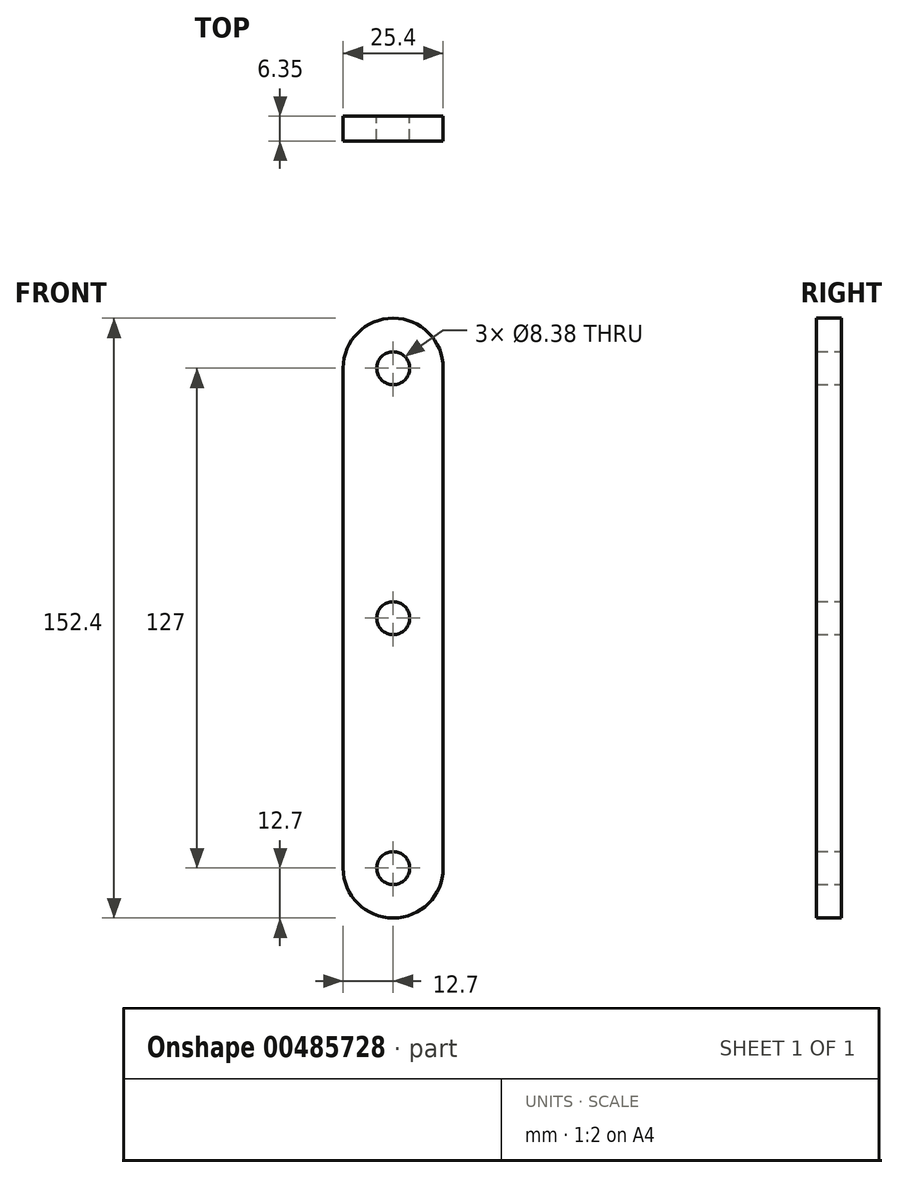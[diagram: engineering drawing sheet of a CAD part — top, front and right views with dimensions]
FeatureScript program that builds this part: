
annotation { "Feature Type Name" : "Feature", "Feature Type Description" : "" }
export const myFeature = defineFeature(function(context is Context, id is Id, definition is map)
    precondition{}
    {
        {
            var Q0;
            Q0=qCreatedBy(makeId("Front.planeOp"),FACE);
            var sketch = newSketch(context, id + "F0", { "sketchPlane" : qUnion([Q0])});
            skLineSegment(sketch, "E0.bottom", {"start": v(12.7, 63.5) * mm, "end": v(-12.7, 63.5) * mm});
            skLineSegment(sketch, "E0.top", {"start": v(12.7, -63.5) * mm, "end": v(-12.7, -63.5) * mm});
            skLineSegment(sketch, "E0.left", {"start": v(12.7, 63.5) * mm, "end": v(12.7, -63.5) * mm});
            skLineSegment(sketch, "E0.right", {"start": v(-12.7, 63.5) * mm, "end": v(-12.7, -63.5) * mm});
            skPoint(sketch, "E0.middle", {"position": v(0, 0) * mm});
            skPoint(sketch, "E1", {"position": v(0, 63.5) * mm});
            skPoint(sketch, "E2", {"position": v(0, -63.5) * mm});
            skCircle(sketch, "E3", {"center": v(0, 63.5) * mm, "radius": 12.7 * mm});
            skCircle(sketch, "E4", {"center": v(0, -63.5) * mm, "radius": 12.7 * mm});
            skCircle(sketch, "E5", {"center": v(0, -63.5) * mm, "radius": 4.2 * mm});
            skCircle(sketch, "E6", {"center": v(0, 0) * mm, "radius": 4.2 * mm});
            skCircle(sketch, "E7", {"center": v(0, 63.5) * mm, "radius": 4.2 * mm});
            skSolve(sketch);
        }
        {
            var Q0;
            {var subQ1=sQuery(id+"F0.wireOp",EDGE,"E0.bottom");var subQ3=sQuery(id+"F0.wireOp",EDGE,"E7");var subQ4=makeQuery(id+"F0.imprint","INTERSECT",VERTEX,{"disambiguationData":[OD(0.0)],"derivedFrom":[subQ1,subQ3]});Q0=makeQuery(id+"F0.imprint","IMPRINT",FACE,{"disambiguationData":[TD([[makeQuery(id+"F0.imprint","IMPRINT",EDGE,{"disambiguationData":[TD([[subQ4,1.0]])],"derivedFrom":subQ3}),-1.0]])]});}
            var Q1;
            {var subQ1=sQuery(id+"F0.wireOp",EDGE,"E0.bottom");var subQ3=sQuery(id+"F0.wireOp",EDGE,"E7");var subQ4=makeQuery(id+"F0.imprint","INTERSECT",VERTEX,{"disambiguationData":[OD(0.0)],"derivedFrom":[subQ1,subQ3]});Q1=makeQuery(id+"F0.imprint","IMPRINT",FACE,{"disambiguationData":[TD([[makeQuery(id+"F0.imprint","IMPRINT",EDGE,{"disambiguationData":[TD([[subQ4,-1.0]])],"derivedFrom":subQ3}),-1.0]])]});}
            var Q2;
            {var subQ1=sQuery(id+"F0.wireOp",EDGE,"E0.left");Q2=makeQuery(id+"F0.imprint","IMPRINT",FACE,{"disambiguationData":[TD([[makeQuery(id+"F0.imprint","IMPRINT",EDGE,{"derivedFrom":subQ1}),-1.0]])]});}
            var Q3;
            {var subQ1=sQuery(id+"F0.wireOp",EDGE,"E0.top");var subQ3=sQuery(id+"F0.wireOp",EDGE,"E5");var subQ4=makeQuery(id+"F0.imprint","INTERSECT",VERTEX,{"disambiguationData":[OD(0.0)],"derivedFrom":[subQ1,subQ3]});Q3=makeQuery(id+"F0.imprint","IMPRINT",FACE,{"disambiguationData":[TD([[makeQuery(id+"F0.imprint","IMPRINT",EDGE,{"disambiguationData":[TD([[subQ4,-1.0]])],"derivedFrom":subQ3}),-1.0]])]});}
            var Q4;
            {var subQ1=sQuery(id+"F0.wireOp",EDGE,"E0.top");var subQ3=sQuery(id+"F0.wireOp",EDGE,"E5");var subQ4=makeQuery(id+"F0.imprint","INTERSECT",VERTEX,{"disambiguationData":[OD(0.0)],"derivedFrom":[subQ1,subQ3]});Q4=makeQuery(id+"F0.imprint","IMPRINT",FACE,{"disambiguationData":[TD([[makeQuery(id+"F0.imprint","IMPRINT",EDGE,{"disambiguationData":[TD([[subQ4,1.0]])],"derivedFrom":subQ3}),-1.0]])]});}
            extrude(context, id + "F1", {"entities" : qUnion([Q0, Q1, Q2, Q3, Q4]), "depth" : 6.35 * mm});
        }
    });
